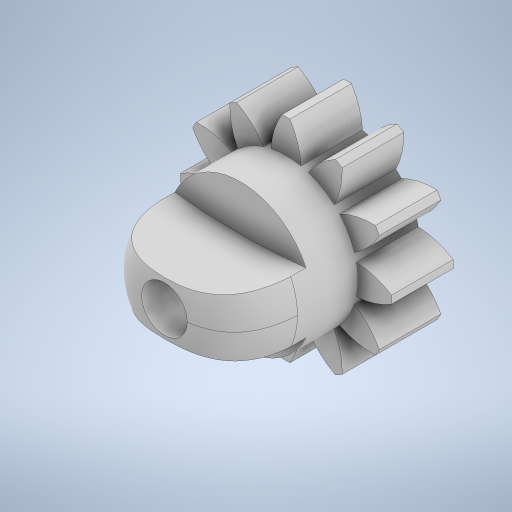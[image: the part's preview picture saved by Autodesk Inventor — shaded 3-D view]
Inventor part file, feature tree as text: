
AUTODESK INVENTOR PART (.ipt)
format: ipt  version: 2023.1 (Build 271208000, 208)  size: 435,200 bytes
history: native  units: mm
features: extrude x8, sketch x6, other x1, pattern_circular x1, revolve x1, projected_geometry x1
ambient origin geometry x8: Origin, YZ Plane, XZ Plane, XY Plane, X Axis, Y Axis, Z Axis, Center Point
bodies: Body1 (feature_tree)
feature tree (18):
  other  "솔리드1"
  sketch  "스케치1"
  extrude  "돌출1"  Depth=24.0mm
  extrude  "돌출2"  Depth=28.0mm
  extrude  "돌출3"  Depth=19.0mm
  extrude  "돌출4"  Depth=1.57mm
  extrude  "돌출6"  Depth=1.0mm
  pattern_circular  "원형 패턴2"  [2 undecoded]
  sketch  "스케치5"
  extrude  "돌출7"  Depth=7.5mm
  extrude  "돌출8"  Depth=4.9mm
  extrude  "돌출9"  Depth=8.1mm TaperAngle=0.0deg
  revolve  "회전1"
  sketch  "스케치2"
  sketch  "스케치4"
  projected_geometry  "투영된 루프2"
  sketch  "스케치6"
  sketch  "스케치7"
note: 2 required parameter values undecoded (feature->parameter linkage not recoverable at this tier; creation-order binding heuristic only, values carry confidence <= 0.55)
